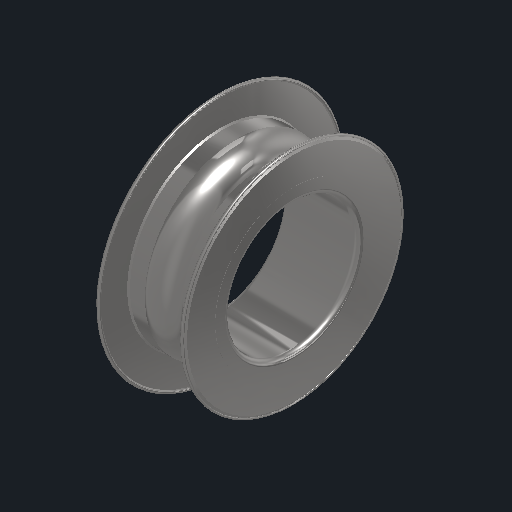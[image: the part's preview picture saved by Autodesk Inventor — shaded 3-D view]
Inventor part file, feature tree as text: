
AUTODESK INVENTOR PART (.ipt)
format: ipt  version: 2022 (Build 260153000, 153)  size: 240,640 bytes
history: native  units: mm (DEFAULTED — no unit token found)
features: revolve x3, sketch x3
ambient origin geometry x8: Origin, YZ Plane, XZ Plane, XY Plane, X Axis, Y Axis, Z Axis, Center Point
bodies: Solid1 (feature_tree)
feature tree (6):
  revolve  "Revolution1"  Angle=360.0deg
  revolve  "Revolution2"  [1 undecoded]
  revolve  "Revolution3"  [1 undecoded]
  sketch  "Sketch_4"  dims[d0=360.0deg d1=360.0deg]
  sketch  "Sketch_5"  dims[d2=360.0deg]
  sketch  "Sketch_6"
note: 2 required parameter values undecoded (feature->parameter linkage not recoverable at this tier; creation-order binding heuristic only, values carry confidence <= 0.55)
